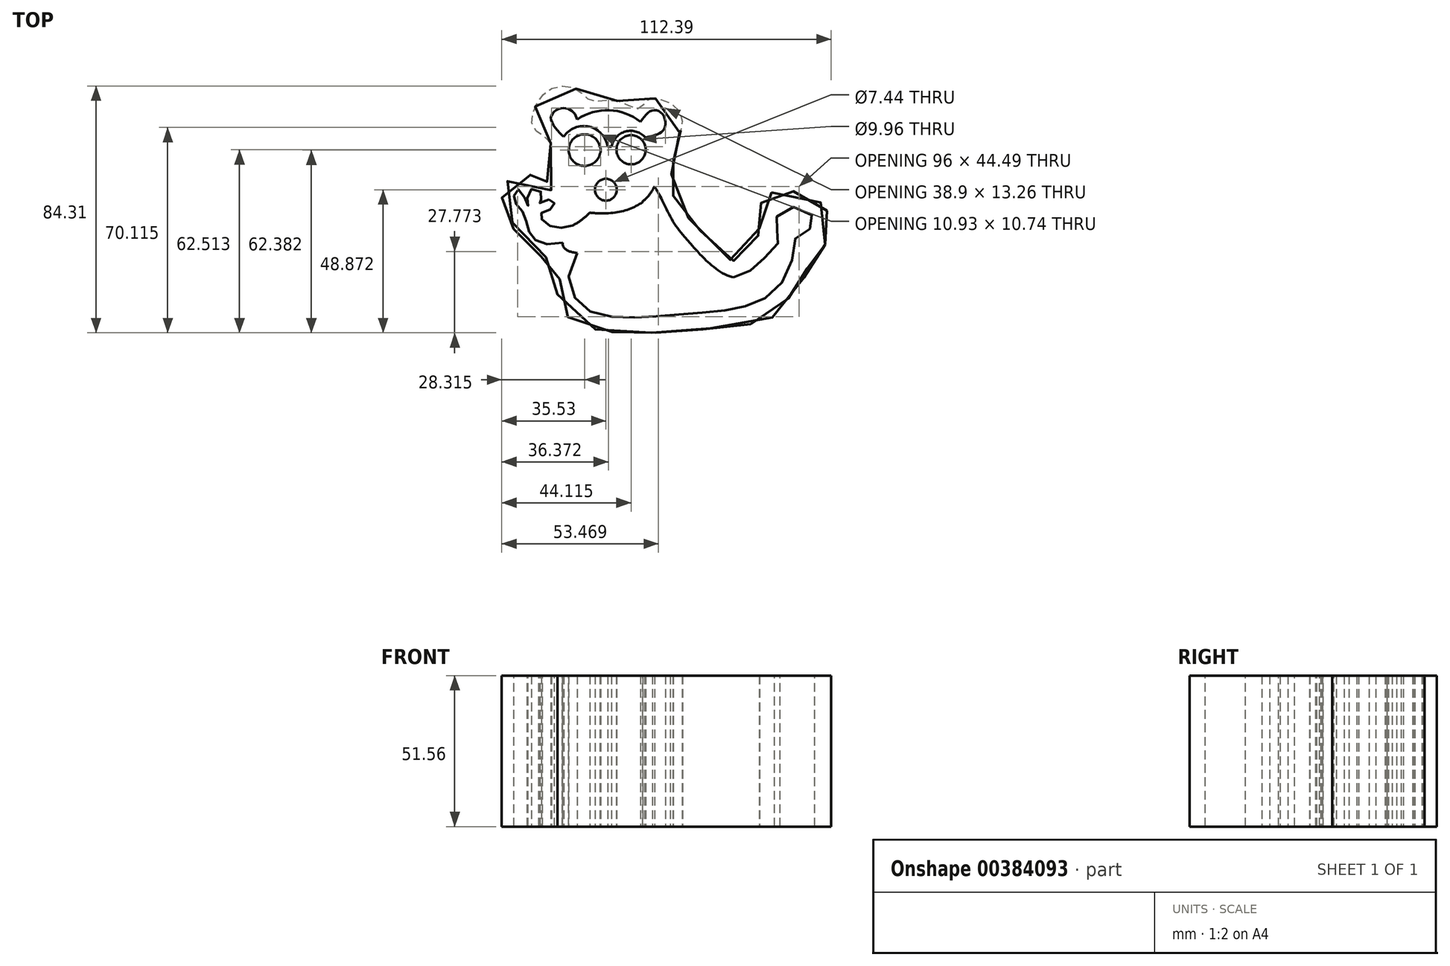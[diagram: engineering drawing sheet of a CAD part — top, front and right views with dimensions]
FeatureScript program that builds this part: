
annotation { "Feature Type Name" : "Feature", "Feature Type Description" : "" }
export const myFeature = defineFeature(function(context is Context, id is Id, definition is map)
    precondition{}
    {
        {
            var Q0;
            Q0=qCreatedBy(makeId("Top.planeOp"),FACE);
            var sketch = newSketch(context, id + "F0", { "sketchPlane" : qUnion([Q0])});
            skArc(sketch, "E0", {"start": v(-21.72, 20.05) * mm, "mid": v(-19.46, 22.53) * mm, "end": v(-17.7, 25.38) * mm});
            skFitSpline(sketch, "E1", {"points": [v(-49.22, 42.73) * mm, v(-53.04, 48.92) * mm, v(-49.99, 51.97) * mm, v(-45.72, 51.05) * mm, v(-44.03, 48.22) * mm], "startDerivative": vector(-19.11, 20.95) * mm, "endDerivative": vector(5.71, -15) * mm});
            skFitSpline(sketch, "E2", {"points": [v(-22.53, 47.4) * mm, v(-18.29, 51.36) * mm, v(-14.63, 49.53) * mm, v(-14.63, 44.65) * mm, v(-18.4, 42.64) * mm], "startDerivative": vector(14.32, 19.65) * mm, "endDerivative": vector(-18.88, -5.22) * mm});
            skArc(sketch, "E3.trimOffspring", {"start": v(-22.53, 47.4) * mm, "mid": v(-33.14, 51.37) * mm, "end": v(-44.03, 48.22) * mm});
            skFitSpline(sketch, "E4.trimOffspring", {"points": [v(-45.72, 12.04) * mm, v(-14.63, 11.73) * mm, v(-21.07, 20.68) * mm, v(-21.75, 20.03) * mm, v(-21.72, 20.05) * mm], "startDerivative": vector(-81.3, -89.09) * mm, "endDerivative": vector(1.85, 13.53) * mm});
            skPoint(sketch, "E5.1.internal.orphan", {"position": v(-103.33, 0) * mm});
            skFitSpline(sketch, "E6", {"points": [v(-39.78, 16.38) * mm, v(-45.72, 12.04) * mm, v(-53.8, 12.04) * mm, v(-56.54, 16) * mm, v(-52.27, 18.14) * mm, v(-52.88, 20.88) * mm, v(-57.15, 19.66) * mm, v(-55.93, 22.7) * mm, v(-60.5, 23.93) * mm, v(-60.8, 18.75) * mm, v(-63.86, 24.23) * mm, v(-65.68, 21.18) * mm, v(-62.64, 16.61) * mm, v(-60.2, 9.3) * mm, v(-52.88, 5.64) * mm, v(-41.3, 7.47) * mm, v(-45.72, 0) * mm, v(-45.72, -11.13) * mm, v(-39.17, -17.53) * mm, v(-28.5, -19.35) * mm, v(-18.14, -19.05) * mm, v(-6.86, -18.14) * mm, v(4.72, -17.22) * mm, v(13.87, -15.4) * mm, v(23.01, -10.52) * mm, v(29.1, 0) * mm, v(31.24, 9) * mm, v(36.73, 12.04) * mm, v(33.38, 17.83) * mm, v(25.15, 16.3) * mm, v(23.32, 12.04) * mm, v(25.15, 8.08) * mm, v(21.49, 2.6) * mm, v(15.7, -2.9) * mm, v(9.3, -5.64) * mm, v(0, 0) * mm, v(-4.72, 5.03) * mm, v(-10.52, 12.04) * mm, v(-15.09, 20.57) * mm, v(-17.7, 25.38) * mm], "startDerivative": vector(-208.45, -194.87) * mm, "endDerivative": vector(-113.32, 198.68) * mm});
            skCircle(sketch, "E7", {"center": v(-34.3, 24.23) * mm, "radius": 3.72 * mm});
            skPoint(sketch, "E8.1.internal.orphan", {"position": v(-58.67, 44.9) * mm});
            skPoint(sketch, "E8.19.internal.orphan", {"position": v(9, 0) * mm});
            skPoint(sketch, "E8.21.internal.orphan", {"position": v(18.14, 12.04) * mm});
            skPoint(sketch, "E8.31.internal.orphan", {"position": v(23.32, -14.17) * mm});
            skPoint(sketch, "E8.32.internal.orphan", {"position": v(23.32, -18.75) * mm});
            skFitSpline(sketch, "E9", {"points": [v(-53.04, 40.08) * mm, v(-58.67, 44.9) * mm, v(-58.67, 51.97) * mm, v(-53.04, 58.67) * mm, v(-44.43, 58.67) * mm, v(-39.47, 54.71) * mm, v(-30.94, 54.71) * mm, v(-23.01, 51.97) * mm, v(-19.66, 55.02) * mm, v(-9.9, 51.97) * mm, v(-8.69, 44.9) * mm, v(-11.13, 39.78) * mm, v(-11.43, 32.16) * mm, v(-12.34, 25.76) * mm, v(-8.38, 17.22) * mm, v(0, 8.08) * mm, v(9, 0) * mm, v(15.4, 3.2) * mm, v(18.14, 12.04) * mm, v(18.14, 17.83) * mm, v(21.18, 22.7) * mm, v(30.33, 23.62) * mm, v(39.17, 19.66) * mm, v(42.52, 12.04) * mm, v(40.7, 5.64) * mm, v(36.12, 3.81) * mm, v(33.99, -4.42) * mm, v(30.02, -9.6) * mm, v(23.32, -18.75) * mm, v(9, -22.4) * mm, v(-3.5, -23.62) * mm, v(-16.92, -24.54) * mm, v(-27.89, -24.54) * mm, v(-40.7, -22.7) * mm, v(-49.99, -16) * mm, v(-49.99, -6.25) * mm, v(-49.99, 0) * mm, v(-63.25, 3.2) * mm, v(-65.99, 12.04) * mm, v(-68.43, 17.22) * mm, v(-69.34, 24.84) * mm, v(-60.5, 29.41) * mm, v(-52.88, 23.93) * mm, v(-56.24, 33.38) * mm, v(-53.04, 40.08) * mm]});
            skPoint(sketch, "E10.3.internal.orphan", {"position": v(-40.39, 40.08) * mm});
            skPoint(sketch, "E10.4.internal.orphan", {"position": v(-39.47, 44.65) * mm});
            skFitSpline(sketch, "E11", {"points": [v(-25.76, 41.91) * mm, v(-18.14, 42.21) * mm], "startDerivative": vector(7.62, 0.3) * mm, "endDerivative": vector(7.62, 0.3) * mm});
            skFitSpline(sketch, "E12", {"points": [v(-51.05, 34.6) * mm, v(-51.05, 25.38) * mm, v(-44.96, 19.35) * mm, v(-39.78, 16.38) * mm], "startDerivative": vector(-4.75, -27.24) * mm, "endDerivative": vector(16.83, -9) * mm});
            skFitSpline(sketch, "E13", {"points": [v(-39.78, 16.38) * mm, v(-21.72, 20.05) * mm], "startDerivative": vector(22.15, -2.22) * mm, "endDerivative": vector(13.7, 9.95) * mm});
            skFitSpline(sketch, "E14", {"points": [v(-37.34, 15.75) * mm, v(-37.34, 16.2) * mm], "startDerivative": vector(0, 0.45) * mm, "endDerivative": vector(0, 0.45) * mm});
            skFitSpline(sketch, "E15", {"points": [v(9.3, -5.64) * mm, v(7.16, -8.08) * mm], "startDerivative": vector(-2.13, -2.44) * mm, "endDerivative": vector(-2.13, -2.44) * mm});
            skFitSpline(sketch, "E16", {"points": [v(-48.99, 38.08) * mm, v(-51.63, 31.32) * mm], "startDerivative": vector(-2.64, -6.77) * mm, "endDerivative": vector(-2.64, -6.77) * mm});
            skFitSpline(sketch, "E17", {"points": [v(-8.13, 8.87) * mm, v(-4.72, 5.03) * mm], "startDerivative": vector(3.4, -3.84) * mm, "endDerivative": vector(3.4, -3.84) * mm});
            skPoint(sketch, "E18.0.internal.orphan", {"position": v(-45.94, 38.28) * mm});
            skPoint(sketch, "E18.1.internal.orphan", {"position": v(-44.94, 38.28) * mm});
            skCircle(sketch, "E19", {"center": v(-25.7, 37.87) * mm, "radius": 4.98 * mm});
            skArc(sketch, "E20", {"start": v(-36.28, 38.85) * mm, "mid": v(-46.97, 37.8) * mm, "end": v(-36.31, 36.48) * mm});
            skArc(sketch, "E21", {"start": v(-33.7, 38.85) * mm, "mid": v(-50.07, 37.8) * mm, "end": v(-33.72, 36.48) * mm});
            skArc(sketch, "E22", {"start": v(-32.32, 36.48) * mm, "mid": v(-25.84, 31.13) * mm, "end": v(-19.36, 36.5) * mm});
            skLineSegment(sketch, "E23.trimOffspring", {"start": v(-33.7, 38.85) * mm, "end": v(-32.35, 38.85) * mm});
            skFitSpline(sketch, "E24", {"points": [v(-36.28, 38.85) * mm, v(-36.08, 38.19) * mm, v(-36.07, 37.32) * mm, v(-36.31, 36.48) * mm], "startDerivative": vector(0.74, -2.04) * mm, "endDerivative": vector(-0.86, -2.36) * mm});
            skLineSegment(sketch, "E25", {"start": v(-33.72, 36.48) * mm, "end": v(-32.32, 36.48) * mm});
            skLineSegment(sketch, "E26", {"start": v(-19.3, 36.5) * mm, "end": v(-16.96, 36.29) * mm});
            skLineSegment(sketch, "E27", {"start": v(-19.36, 36.5) * mm, "end": v(-19.3, 36.5) * mm});
            skLineSegment(sketch, "E28", {"start": v(-19.36, 36.5) * mm, "end": v(-19.36, 36.5) * mm});
            skArc(sketch, "E29.trimOffspring", {"start": v(-20.83, 42.03) * mm, "mid": v(-27.6, 44.1) * mm, "end": v(-32.35, 38.85) * mm});
            skFitSpline(sketch, "E30", {"points": [v(-37.34, 16.2) * mm, v(-32.4, 15.64) * mm], "startDerivative": vector(1.6, -0.17) * mm, "endDerivative": vector(1.6, -0.17) * mm});
            skFitSpline(sketch, "E31", {"points": [v(-49.22, 42.73) * mm, v(-48.68, 42.3) * mm], "startDerivative": vector(0.54, -0.43) * mm, "endDerivative": vector(0.54, -0.43) * mm});
            skFitSpline(sketch, "E32", {"points": [v(-18.4, 42.64) * mm, v(-20.68, 42.11) * mm], "startDerivative": vector(-2.28, -0.53) * mm, "endDerivative": vector(-2.28, -0.53) * mm});
            skFitSpline(sketch, "E33", {"points": [v(-20.68, 42.11) * mm, v(-20.83, 42.03) * mm], "startDerivative": vector(-0.16, -0.09) * mm, "endDerivative": vector(-0.16, -0.09) * mm});
            skPoint(sketch, "E34.orphan", {"position": v(-19.53, 39.65) * mm});
            skPoint(sketch, "E35.endDerivative.orphan", {"position": v(-16.91, 39.65) * mm});
            skPoint(sketch, "E36.1.internal.snap0", {"position": v(-18.13, 36.4) * mm});
            skPoint(sketch, "E36.2.internal.snap0", {"position": v(-18.13, 36.4) * mm});
            skPoint(sketch, "E36.1.internal.orphan", {"position": v(-18.13, 32.96) * mm});
            skPoint(sketch, "E36.2.internal.orphan", {"position": v(-18.13, 28.38) * mm});
            skFitSpline(sketch, "E37", {"points": [v(-36.8, 16.14) * mm, v(-36.8, 8.99) * mm, v(-39.78, 0) * mm, v(-39.78, -10.46) * mm, v(-30.85, -13.95) * mm, v(-13.82, -14.83) * mm, v(0, -13.73) * mm, v(8.9, -11.99) * mm, v(-5.08, -4.12) * mm, v(-17.31, 6.58) * mm, v(-21.72, 20.05) * mm], "startDerivative": vector(9.05, -92.74) * mm, "endDerivative": vector(-29.63, 131.96) * mm});
            skPoint(sketch, "E38", {"position": v(-66.43, 51.04) * mm});
            skPoint(sketch, "E39", {"position": v(-55.19, 16.45) * mm});
            skPoint(sketch, "E40", {"position": v(-11.03, 21.23) * mm});
            skPoint(sketch, "E41", {"position": v(-36.34, -1.55) * mm});
            skPoint(sketch, "E42", {"position": v(-31.56, -1.27) * mm});
            skPoint(sketch, "E43", {"position": v(-28.75, -8.02) * mm});
            skPoint(sketch, "E44", {"position": v(-30.16, 3.52) * mm});
            skPoint(sketch, "E45", {"position": v(-15.53, -8.02) * mm});
            skPoint(sketch, "E46", {"position": v(-25.38, -9.14) * mm});
            skPoint(sketch, "E47", {"position": v(-26.78, -4.36) * mm});
            skPoint(sketch, "E48", {"position": v(-18.9, -12.8) * mm});
            skPoint(sketch, "E49", {"position": v(-21.16, -13.64) * mm});
            skPoint(sketch, "E50", {"position": v(-29.03, -7.45) * mm});
            skPoint(sketch, "E51", {"position": v(-27.34, -4.92) * mm});
            skPoint(sketch, "E52", {"position": v(-35.78, -6.05) * mm});
            skPoint(sketch, "E53", {"position": v(-39.44, -8.02) * mm});
            skPoint(sketch, "E54", {"position": v(-39.44, -8.3) * mm});
            skPoint(sketch, "E55", {"position": v(-40, -8.86) * mm});
            skPoint(sketch, "E56", {"position": v(-43.66, -11.67) * mm});
            skPoint(sketch, "E57", {"position": v(-43.94, -11.95) * mm});
            skPoint(sketch, "E58", {"position": v(-48.44, -14.48) * mm});
            skPoint(sketch, "E59", {"position": v(-51.53, -15.89) * mm});
            skSolve(sketch);
        }
        {
            var Q0;
            Q0 = qSketchRegion(id + "F0", true);
            extrude(context, id + "F1", {"entities" : qUnion([Q0]), "depth" : 51.56 * mm});
        }
    });
